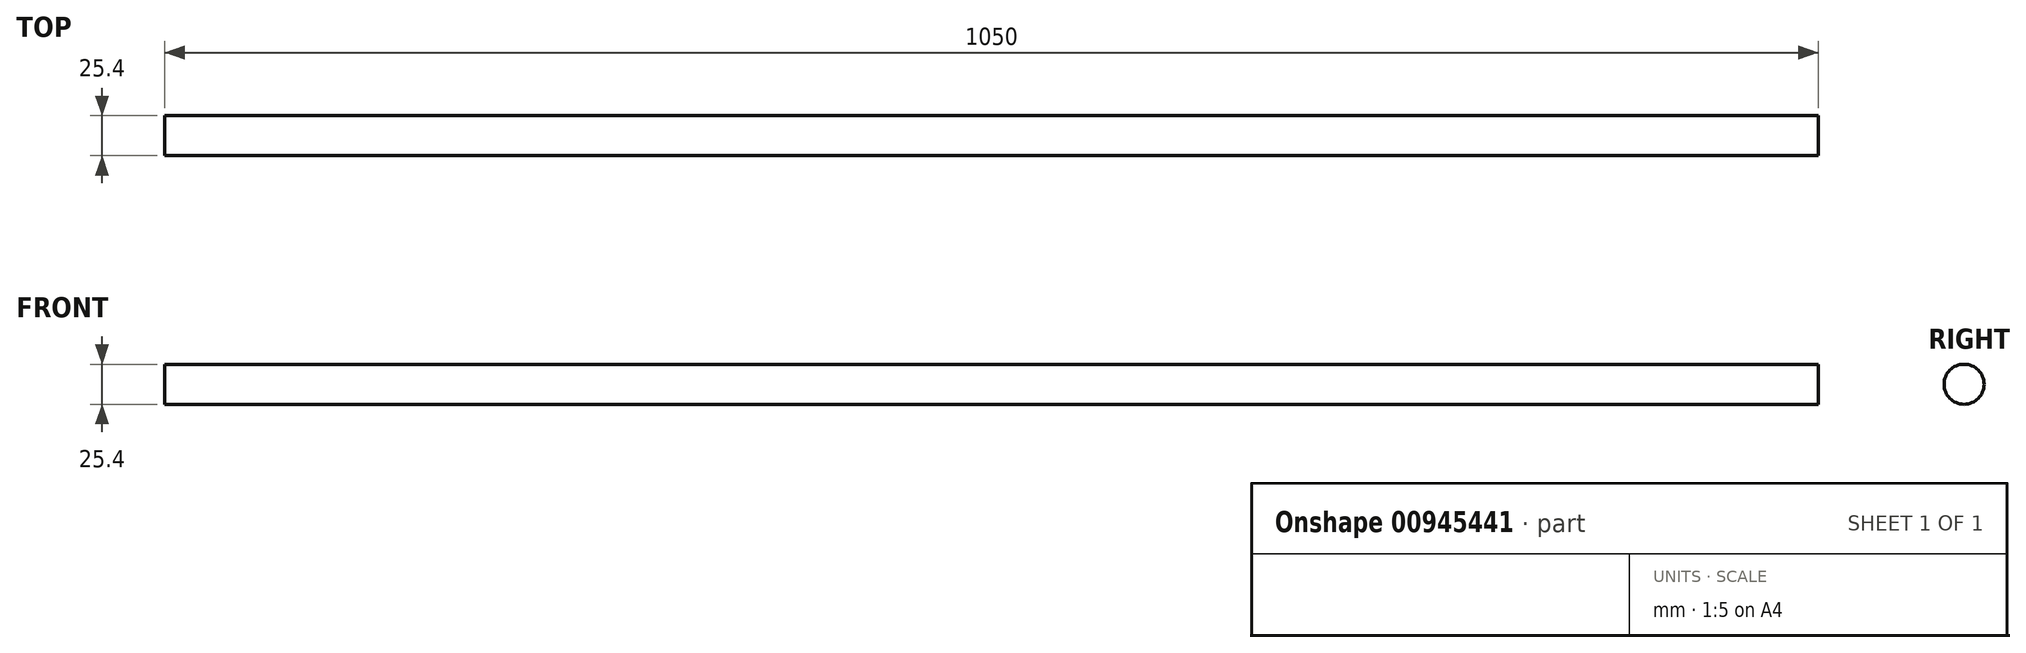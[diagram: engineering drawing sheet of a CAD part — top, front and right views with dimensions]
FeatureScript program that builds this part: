
annotation { "Feature Type Name" : "Feature", "Feature Type Description" : "" }
export const myFeature = defineFeature(function(context is Context, id is Id, definition is map)
    precondition{}
    {
        {
            var Q0;
            Q0=qCreatedBy(makeId("Right.planeOp"),FACE);
            var sketch = newSketch(context, id + "F0", { "sketchPlane" : qUnion([Q0])});
            skCircle(sketch, "E0", {"center": v(0, 0) * mm, "radius": 12.7 * mm});
            skSolve(sketch);
        }
        {
            var Q0;
            Q0=sQuery(id+"F0.wireOp",EDGE,"E0");
            extrude(context, id + "F1", {"bodyType" : ToolBodyType.SURFACE, "surfaceEntities" : qUnion([Q0]), "depth" : 1050 * mm, "offsetDistance" : 25.4 * mm});
        }
    });
